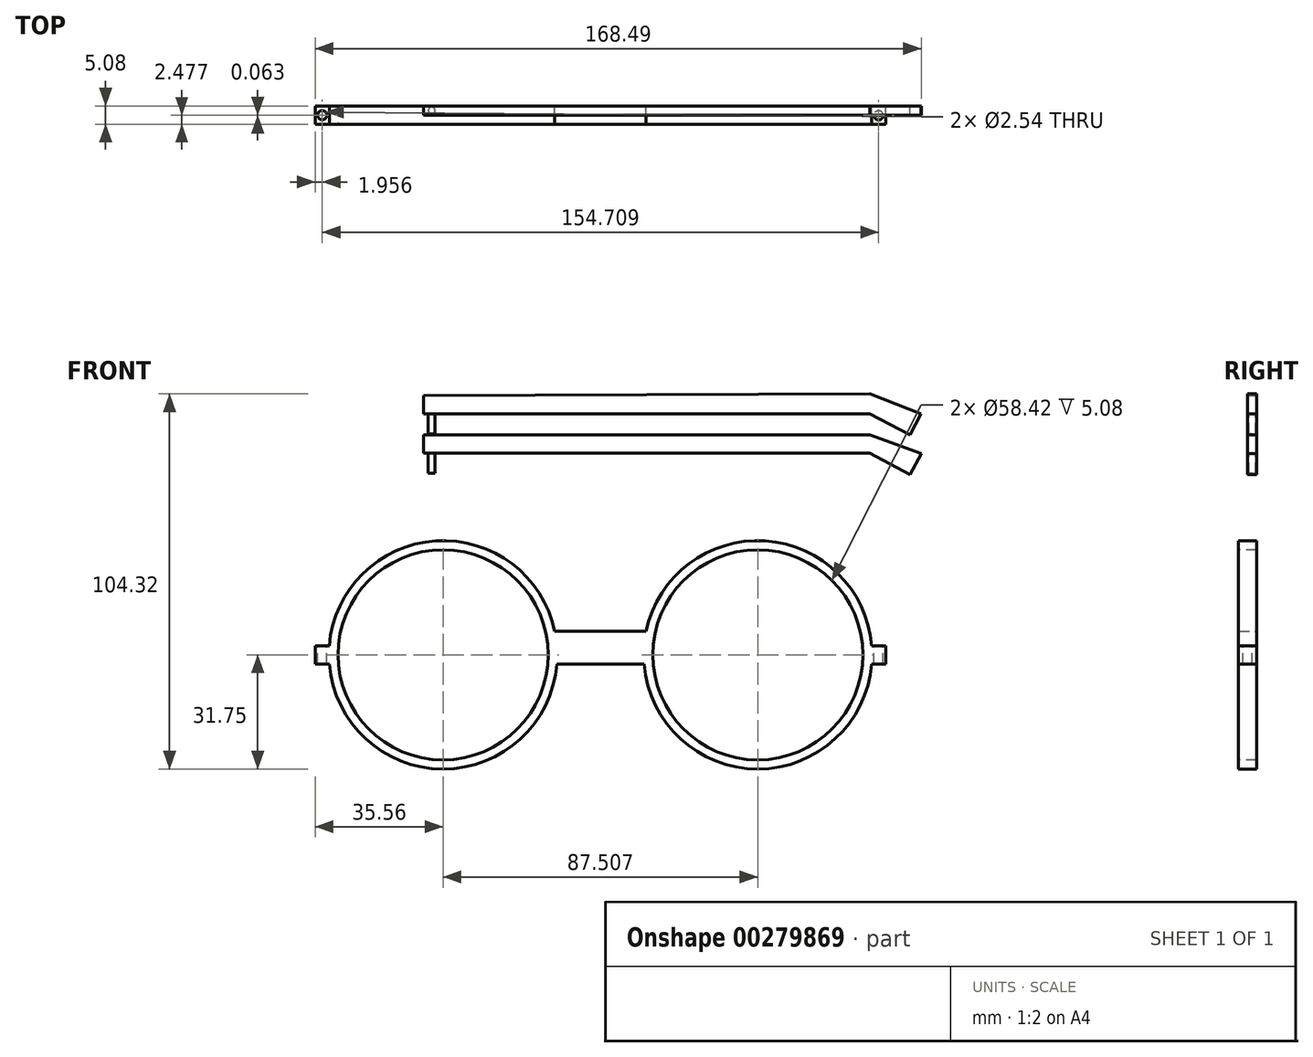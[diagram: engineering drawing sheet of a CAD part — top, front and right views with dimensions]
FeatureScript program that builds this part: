
annotation { "Feature Type Name" : "Feature", "Feature Type Description" : "" }
export const myFeature = defineFeature(function(context is Context, id is Id, definition is map)
    precondition{}
    {
        {
            var Q0;
            Q0=qCreatedBy(makeId("Front.planeOp"),FACE);
            var sketch = newSketch(context, id + "F0", { "sketchPlane" : qUnion([Q0])});
            skCircle(sketch, "E0", {"center": v(-35.37, 0) * mm, "radius": 31.75 * mm});
            skCircle(sketch, "E1", {"center": v(52.14, 0) * mm, "radius": 31.75 * mm});
            skLineSegment(sketch, "E2", {"start": v(-4.32, 6.61) * mm, "end": v(21.08, 6.61) * mm});
            skLineSegment(sketch, "E3", {"start": v(21.08, 6.61) * mm, "end": v(20.5, -2.61) * mm});
            skLineSegment(sketch, "E4", {"start": v(20.5, -2.61) * mm, "end": v(-3.73, -2.61) * mm});
            skLineSegment(sketch, "E5", {"start": v(-3.73, -2.61) * mm, "end": v(-4.32, 6.61) * mm});
            skLineSegment(sketch, "E6.bottom", {"start": v(87.7, 2.54) * mm, "end": v(80.08, 2.54) * mm});
            skLineSegment(sketch, "E6.top", {"start": v(87.7, -2.54) * mm, "end": v(80.08, -2.54) * mm});
            skLineSegment(sketch, "E6.left", {"start": v(87.7, 2.54) * mm, "end": v(87.7, -2.54) * mm});
            skLineSegment(sketch, "E6.right", {"start": v(80.08, 2.54) * mm, "end": v(80.08, -2.54) * mm});
            skPoint(sketch, "E6.middle", {"position": v(83.89, 0) * mm});
            skLineSegment(sketch, "E7.bottom", {"start": v(-70.93, -2.54) * mm, "end": v(-63.3, -2.54) * mm});
            skLineSegment(sketch, "E7.top", {"start": v(-70.93, 2.54) * mm, "end": v(-63.3, 2.54) * mm});
            skLineSegment(sketch, "E7.left", {"start": v(-70.93, -2.54) * mm, "end": v(-70.93, 2.54) * mm});
            skLineSegment(sketch, "E7.right", {"start": v(-63.3, -2.54) * mm, "end": v(-63.3, 2.54) * mm});
            skPoint(sketch, "E7.middle", {"position": v(-67.12, 0) * mm});
            skSolve(sketch);
        }
        {
            var Q0;
            Q0 = qSketchRegion(id + "F0", true);
            extrude(context, id + "F1", {"entities" : qUnion([Q0]), "depth" : 5.08 * mm});
        }
        {
            var Q0;
            Q0=makeQuery(id+"F1.opExtrude","CAP_FACE",FACE,{"disambiguationData":[OSD([sQuery(id+"F0.wireOp",EDGE,"E0"),sQuery(id+"F0.wireOp",EDGE,"E1"),sQuery(id+"F0.wireOp",EDGE,"E2"),sQuery(id+"F0.wireOp",EDGE,"E4"),sQuery(id+"F0.wireOp",EDGE,"E6.bottom"),sQuery(id+"F0.wireOp",EDGE,"E6.top"),sQuery(id+"F0.wireOp",EDGE,"E6.left"),sQuery(id+"F0.wireOp",EDGE,"E7.bottom"),sQuery(id+"F0.wireOp",EDGE,"E7.top"),sQuery(id+"F0.wireOp",EDGE,"E7.left")])],"isStart":false});
            var sketch = newSketch(context, id + "F2", { "sketchPlane" : qUnion([Q0])});
            skCircle(sketch, "E8", {"center": v(-35.37, 0) * mm, "radius": 29.21 * mm});
            skCircle(sketch, "E9", {"center": v(52.14, 0) * mm, "radius": 29.21 * mm});
            skSolve(sketch);
        }
        {
            var Q0;
            Q0 = qSketchRegion(id + "F2", true);
            extrude(context, id + "F3", {"entities" : qUnion([Q0]), "operationType" : NewBodyOperationType.REMOVE, "oppositeDirection" : true, "depth" : 25.4 * mm});
        }
        {
            var Q0;
            Q0=makeQuery(id+"F1.opExtrude","SWEPT_FACE",FACE,{"disambiguationData":[OSD([sQuery(id+"F0.wireOp",EDGE,"E6.bottom")])]});
            var sketch = newSketch(context, id + "F4", { "sketchPlane" : qUnion([Q0])});
            skCircle(sketch, "E10", {"center": v(-68.97, -2.54) * mm, "radius": 1.27 * mm});
            skPoint(sketch, "E10.centerSnap0", {"position": v(-68.97, 0) * mm});
            skPoint(sketch, "E10.centerSnap1", {"position": v(-67.02, -2.54) * mm});
            skCircle(sketch, "E11", {"center": v(85.74, -2.6) * mm, "radius": 1.27 * mm});
            skSolve(sketch);
        }
        {
            var Q0;
            Q0 = qSketchRegion(id + "F4", true);
            extrude(context, id + "F5", {"entities" : qUnion([Q0]), "operationType" : NewBodyOperationType.REMOVE, "oppositeDirection" : true, "depth" : 25.4 * mm});
        }
        {
            var Q0;
            Q0=qCreatedBy(makeId("Front.planeOp"),FACE);
            var sketch = newSketch(context, id + "F6", { "sketchPlane" : qUnion([Q0])});
            skLineSegment(sketch, "E12", {"start": v(-40.75, 72.1) * mm, "end": v(-40.75, 67.02) * mm});
            skLineSegment(sketch, "E13", {"start": v(-40.75, 67.02) * mm, "end": v(83.25, 67.02) * mm});
            skLineSegment(sketch, "E14", {"start": v(83.25, 67.02) * mm, "end": v(83.25, 72.57) * mm});
            skLineSegment(sketch, "E15", {"start": v(83.25, 72.57) * mm, "end": v(-40.75, 72.1) * mm});
            skLineSegment(sketch, "E16", {"start": v(83.25, 67.02) * mm, "end": v(94.45, 61.17) * mm});
            skLineSegment(sketch, "E17", {"start": v(94.45, 61.17) * mm, "end": v(97.5, 67.02) * mm});
            skLineSegment(sketch, "E18", {"start": v(97.5, 67.02) * mm, "end": v(83.25, 72.57) * mm});
            skLineSegment(sketch, "E19", {"start": v(-40.75, 61.17) * mm, "end": v(-40.75, 56.1) * mm});
            skPoint(sketch, "E19.startSnap0", {"position": v(-40.75, 69.56) * mm});
            skLineSegment(sketch, "E20", {"start": v(-40.75, 56.1) * mm, "end": v(83.25, 56.1) * mm});
            skLineSegment(sketch, "E21", {"start": v(83.25, 56.1) * mm, "end": v(83.25, 61.17) * mm});
            skLineSegment(sketch, "E22", {"start": v(83.25, 61.17) * mm, "end": v(-40.75, 61.17) * mm});
            skLineSegment(sketch, "E23", {"start": v(83.25, 56.1) * mm, "end": v(94.45, 50.11) * mm});
            skLineSegment(sketch, "E24", {"start": v(94.45, 50.11) * mm, "end": v(97.56, 55.94) * mm});
            skLineSegment(sketch, "E25", {"start": v(97.56, 55.94) * mm, "end": v(83.25, 61.17) * mm});
            skSolve(sketch);
        }
        {
            var Q0;
            Q0 = qSketchRegion(id + "F6", true);
            extrude(context, id + "F7", {"entities" : qUnion([Q0]), "depth" : 2.54 * mm});
        }
        {
            var Q0;
            Q0=makeQuery(id+"F7.opExtrude","SWEPT_FACE",FACE,{"disambiguationData":[OSD([sQuery(id+"F6.wireOp",EDGE,"E13")])]});
            var sketch = newSketch(context, id + "F8", { "sketchPlane" : qUnion([Q0])});
            skCircle(sketch, "E26", {"center": v(-38.53, 1.27) * mm, "radius": 0.95 * mm});
            skPoint(sketch, "E26.centerSnap0", {"position": v(-40.75, 1.27) * mm});
            skSolve(sketch);
        }
        {
            var Q0;
            Q0 = qSketchRegion(id + "F8", true);
            extrude(context, id + "F9", {"entities" : qUnion([Q0]), "operationType" : NewBodyOperationType.ADD, "depth" : 5.6 * mm});
        }
        {
            var Q0;
            Q0=makeQuery(id+"F7.opExtrude","SWEPT_FACE",FACE,{"disambiguationData":[OSD([sQuery(id+"F6.wireOp",EDGE,"E20")])]});
            var sketch = newSketch(context, id + "F10", { "sketchPlane" : qUnion([Q0])});
            skCircle(sketch, "E27", {"center": v(-38.53, 1.27) * mm, "radius": 0.95 * mm});
            skPoint(sketch, "E27.centerSnap0", {"position": v(-40.75, 1.27) * mm});
            skSolve(sketch);
        }
        {
            var Q0;
            Q0 = qSketchRegion(id + "F10", true);
            extrude(context, id + "F11", {"entities" : qUnion([Q0]), "operationType" : NewBodyOperationType.ADD, "depth" : 5.6 * mm});
        }
    });
